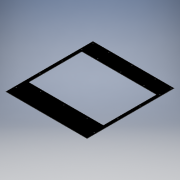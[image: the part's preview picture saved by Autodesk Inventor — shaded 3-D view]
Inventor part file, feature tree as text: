
AUTODESK INVENTOR PART (.ipt)
format: ipt  version: 2017.3 (Build 213256000, 256)  size: 164,864 bytes
history: native  units: mm
features: sheet_metal_op x1, fillet x1, sketch x1, other x1
ambient origin geometry x8: Origin, YZ Plane, XZ Plane, XY Plane, X Axis, Y Axis, Z Axis, Center Point
bodies: Body1 (feature_tree)
feature tree (4):
  sheet_metal_op  "Face4"
  fillet  "Fillet1"  Radius=513.0mm
  sketch  "Sketch1"  dims[d1=550.0mm d2=10.0mm d3=10.0mm d4=10.0mm d5=110.0mm d6=80.0mm d7=110.0mm d8=110.0mm d9=70.0mm d10=55.0mm d11=4.2mm d12=1.5mm d13=1.5mm d14=10.0mm d15=10.0mm d16=1.5mm d17=13.0mm d18=10.0mm d19=1.5mm d20=5.0mm]
  other  "Plate4"
